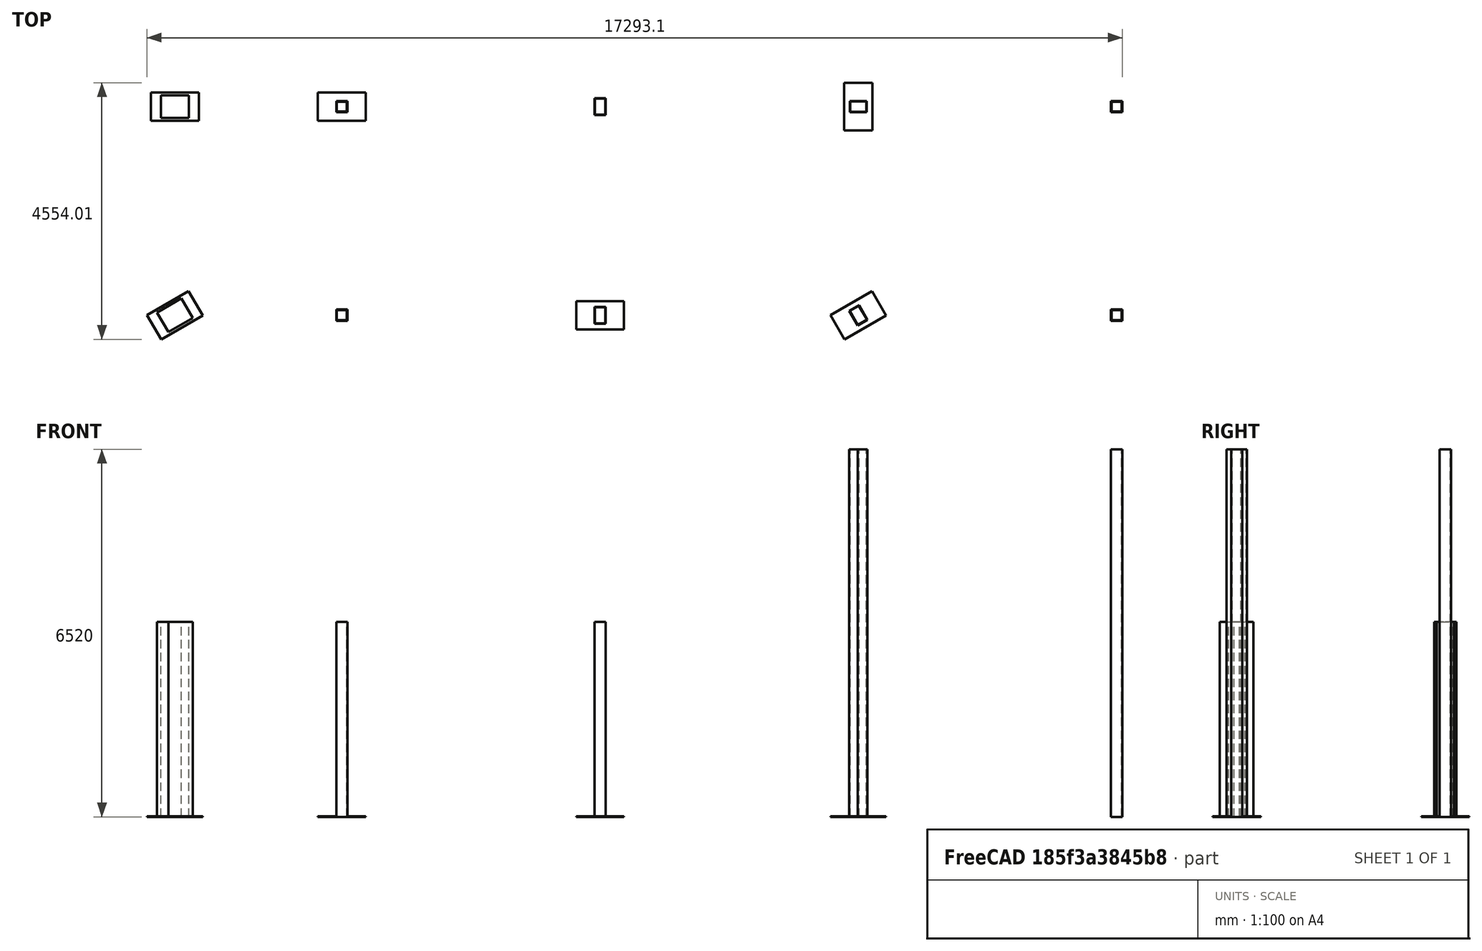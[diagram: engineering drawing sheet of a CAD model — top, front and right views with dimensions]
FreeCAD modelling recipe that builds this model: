
FCSTD DOCUMENT  (FreeCAD 1.0R1234)
Label: base_plate
License: All rights reserved
LicenseURL: http://en.wikipedia.org/wiki/All_rights_reserved
objects: Part::FeaturePython×34, Part::Part2DObjectPython×21, App::FeaturePython×10, App::DocumentObjectGroup×2
note: 147 computed .brp shape members not serialized (recipe doc carries the construction recipe); baked Part::Feature solids carry a one-line shape summary decoded from their .brp

FEATURE [Part::Part2DObjectPython] Line  label="C1_Story1_CenterLine"  # Draft 2D object (typed FeaturePython)
  Area = 0
  ChamferSize = 0
  Closed = false
  End = (30830,27720,3460)
  FilletRadius = 0
  Length = 3460
  MakeFace = true
  Points = (2) [(30830,27720,0),(30830,27720,3460)]
  Start = (30830,27720,0)
  Subdivisions = 0
FEATURE [Part::Part2DObjectPython] COL60X90  # Draft 2D object (typed FeaturePython)
  Height = 500
  Width = 400
FEATURE [Part::Part2DObjectPython] Line001  label="C2_Story1_CenterLine"  # Draft 2D object (typed FeaturePython)
  Area = 0
  ChamferSize = 0
  Closed = false
  End = (30830,31420,3460)
  FilletRadius = 0
  Length = 3460
  MakeFace = true
  Points = (2) [(30830,31420,0),(30830,31420,3460)]
  Start = (30830,31420,0)
  Subdivisions = 0
FEATURE [Part::Part2DObjectPython] Line002  label="C3_Story1_CenterLine"  # Draft 2D object (typed FeaturePython)
  Area = 0
  ChamferSize = 0
  Closed = false
  End = (33790,27720,3460)
  FilletRadius = 0
  Length = 3460
  MakeFace = true
  Points = (2) [(33790,27720,0),(33790,27720,3460)]
  Start = (33790,27720,0)
  Subdivisions = 0
FEATURE [Part::Part2DObjectPython] BOX200X200X12  # Draft 2D object (typed FeaturePython)
  Height = 200
  Thickness = 12
  Width = 200
FEATURE [Part::FeaturePython] Structure002  label="C3_Story1"  # Arch/BIM 24 (typed FeaturePython)
  AttacherType = Attacher::AttachEngine3D
  AttachmentOffset = pos=(0,0,0) rot=(0,0,1;1.5708rad)
  Base = -> BOX200X200X12
  BaseMirror = false
  BaseOffsetX = 0
  BaseOffsetY = 0
  BasePerpendicularToTool = false
  BaseRotation = 0
  ComputedLength = 0
  FaceMaker = 0
  Height = 3460
  HorizontalArea = 9024
  IfcData = attributes={"GlobalId": {"name": "GlobalId", "type": "IfcGloballyUniqueId", "is_enum": false, "enum_values": []}, "Description": {"... (+438 chars omitted),+1 more (map truncated)
  IfcType = 24
  Length = 0
  MapMode = 7
  MoveBase = false
  MoveWithHost = false
  Nodes = (2) [(33790,27720,0),(33790,27720,3460)]
  NodesOffset = 0
  Normal = (0,0,0)
  PerimeterLength = 800
  Placement = pos=(33790,27720,0) rot=(0,0,1;1.5708rad)
  PredefinedType = 0
  Support = -> [Line002]
  ToolOffsetFirst = 0
  ToolOffsetLast = 0
  VerticalArea = 5.20384e+06
  Width = 778
  combos_load = DStlD1=225.648, -2449.4, 2.69,DStlD2=273.2928, -3371.06, -126.35,comb11=315.9072, -3429.16, 3.76,comb21=313.3562, -2587.55, 10.91,+37 more (map truncated)
FEATURE [Part::Part2DObjectPython] Line003  label="C4_Story1_CenterLine"  # Draft 2D object (typed FeaturePython)
  Area = 0
  ChamferSize = 0
  Closed = false
  End = (33790,31420,3460)
  FilletRadius = 0
  Length = 3460
  MakeFace = true
  Points = (2) [(33790,31420,0),(33790,31420,3460)]
  Start = (33790,31420,0)
  Subdivisions = 0
FEATURE [Part::Part2DObjectPython] Line004  label="C5_Story1_CenterLine"  # Draft 2D object (typed FeaturePython)
  Area = 0
  ChamferSize = 0
  Closed = false
  End = (38370,27720,3460)
  FilletRadius = 0
  Length = 3460
  MakeFace = true
  Points = (2) [(38370,27720,0),(38370,27720,3460)]
  Start = (38370,27720,0)
  Subdivisions = 0
FEATURE [Part::Part2DObjectPython] BOX20X30  # Draft 2D object (typed FeaturePython)
  Height = 200
  Thickness = 8
  Width = 300
FEATURE [Part::Part2DObjectPython] Line005  label="C6_Story1_CenterLine"  # Draft 2D object (typed FeaturePython)
  Area = 0
  ChamferSize = 0
  Closed = false
  End = (38370,31420,3460)
  FilletRadius = 0
  Length = 3460
  MakeFace = true
  Points = (2) [(38370,31420,0),(38370,31420,3460)]
  Start = (38370,31420,0)
  Subdivisions = 0
FEATURE [Part::FeaturePython] Structure005  label="C6_Story1"  # Arch/BIM 24 (typed FeaturePython)
  AttacherType = Attacher::AttachEngine3D
  AttachmentOffset = pos=(0,0,0) rot=(0,0,1;1.5708rad)
  Base = -> BOX20X30
  BaseMirror = false
  BaseOffsetX = 0
  BaseOffsetY = 0
  BasePerpendicularToTool = false
  BaseRotation = 0
  ComputedLength = 0
  FaceMaker = 0
  Height = 3460
  HorizontalArea = 7744
  IfcData = attributes={"GlobalId": {"name": "GlobalId", "type": "IfcGloballyUniqueId", "is_enum": false, "enum_values": []}, "Description": {"... (+438 chars omitted),+1 more (map truncated)
  IfcType = 24
  Length = 0
  MapMode = 7
  MoveBase = false
  MoveWithHost = false
  Nodes = (2) [(38370,31420,0),(38370,31420,3460)]
  NodesOffset = 0
  Normal = (0,0,0)
  PerimeterLength = 1000
  Placement = pos=(38370,31420,0) rot=(0,0,1;1.5708rad)
  PredefinedType = 0
  Support = -> [Line005]
  ToolOffsetFirst = 0
  ToolOffsetLast = 0
  VerticalArea = 6.69856e+06
  Width = 778
  combos_load = DStlD1=197.8429, 3076.07, 349.51,DStlD2=245.2578, 4878.87, 1107.77,comb11=276.98, 4306.5, 489.31,comb21=243.6131, 3588.13, 163,+37 more (map truncated)
FEATURE [Part::Part2DObjectPython] Line006  label="C11_Story2_CenterLine"  # Draft 2D object (typed FeaturePython)
  Area = 0
  ChamferSize = 0
  Closed = false
  End = (42950,27720,6520)
  FilletRadius = 0
  Length = 6520
  MakeFace = true
  Points = (2) [(42950,27720,0),(42950,27720,6520)]
  Start = (42950,27720,0)
  Subdivisions = 0
FEATURE [Part::Part2DObjectPython] Line007  label="C12_Story2_CenterLine"  # Draft 2D object (typed FeaturePython)
  Area = 0
  ChamferSize = 0
  Closed = false
  End = (42950,31420,6520)
  FilletRadius = 0
  Length = 6520
  MakeFace = true
  Points = (2) [(42950,31420,0),(42950,31420,6520)]
  Start = (42950,31420,0)
  Subdivisions = 0
FEATURE [Part::Part2DObjectPython] Line008  label="C13_Story2_CenterLine"  # Draft 2D object (typed FeaturePython)
  Area = 0
  ChamferSize = 0
  Closed = false
  End = (47530,27720,6520)
  FilletRadius = 0
  Length = 6520
  MakeFace = true
  Points = (2) [(47530,27720,0),(47530,27720,6520)]
  Start = (47530,27720,0)
  Subdivisions = 0
FEATURE [Part::FeaturePython] Structure008  label="C13_Story2"  # Arch/BIM 24 (typed FeaturePython)
  AttacherType = Attacher::AttachEngine3D
  AttachmentOffset = pos=(0,0,0) rot=(0,0,1;3.14159rad)
  Base = -> BOX200X200X12
  BaseMirror = false
  BaseOffsetX = 0
  BaseOffsetY = 0
  BasePerpendicularToTool = false
  BaseRotation = 0
  ComputedLength = 0
  FaceMaker = 0
  Height = 6520
  HorizontalArea = 9024
  IfcData = attributes={"GlobalId": {"name": "GlobalId", "type": "IfcGloballyUniqueId", "is_enum": false, "enum_values": []}, "Description": {"... (+438 chars omitted),+1 more (map truncated)
  IfcType = 24
  Length = 0
  MapMode = 7
  MoveBase = false
  MoveWithHost = false
  Nodes = (2) [(47530,27720,0),(47530,27720,6520)]
  NodesOffset = 0
  Normal = (0,0,0)
  PerimeterLength = 800
  Placement = pos=(47530,27720,0) rot=(0,0,1;3.14159rad)
  PredefinedType = 0
  Support = -> [Line008]
  ToolOffsetFirst = 0
  ToolOffsetLast = 0
  VerticalArea = 9806080
  Width = 778
  combos_load = DStlD1=130.4832, -1568.85, -477.1,DStlD2=152.9529, -2563.65, 493.5,comb11=182.6765, -2196.39, -667.94,comb21=161.6057, -1832.03, -693.36,+37 more (map truncated)
FEATURE [Part::Part2DObjectPython] Line009  label="C14_Story2_CenterLine"  # Draft 2D object (typed FeaturePython)
  Area = 0
  ChamferSize = 0
  Closed = false
  End = (47530,31420,6520)
  FilletRadius = 0
  Length = 6520
  MakeFace = true
  Points = (2) [(47530,31420,0),(47530,31420,6520)]
  Start = (47530,31420,0)
  Subdivisions = 0
FEATURE [Part::FeaturePython] Structure009  label="C14_Story2"  # Arch/BIM 24 (typed FeaturePython)
  AttacherType = Attacher::AttachEngine3D
  AttachmentOffset = pos=(0,0,0) rot=(0,0,1;1.5708rad)
  Base = -> BOX200X200X12
  BaseMirror = false
  BaseOffsetX = 0
  BaseOffsetY = 0
  BasePerpendicularToTool = false
  BaseRotation = 0
  ComputedLength = 0
  FaceMaker = 0
  Height = 6520
  HorizontalArea = 9024
  IfcData = attributes={"GlobalId": {"name": "GlobalId", "type": "IfcGloballyUniqueId", "is_enum": false, "enum_values": []}, "Description": {"... (+438 chars omitted),+1 more (map truncated)
  IfcType = 24
  Length = 0
  MapMode = 7
  MoveBase = false
  MoveWithHost = false
  Nodes = (2) [(47530,31420,0),(47530,31420,6520)]
  NodesOffset = 0
  Normal = (0,0,0)
  PerimeterLength = 800
  Placement = pos=(47530,31420,0) rot=(0,0,1;1.5708rad)
  PredefinedType = 0
  Support = -> [Line009]
  ToolOffsetFirst = 0
  ToolOffsetLast = 0
  VerticalArea = 9.80608e+06
  Width = 778
  combos_load = DStlD1=130.648, 2043.72, -433.08,DStlD2=153.3261, 3531.07, 565.05,comb11=182.9072, 2861.2, -606.31,comb21=161.7518, 2254.87, -666.26,+37 more (map truncated)
FEATURE [Part::Part2DObjectPython] Line010  # Draft 2D object (typed FeaturePython)
  Area = 0
  ChamferSize = 0
  Closed = false
  End = (47530,31420,0)
  FilletRadius = 0
  Length = 16700
  MakeFace = true
  Points = (2) [(30830,31420,0),(47530,31420,0)]
  Start = (30830,31420,0)
  Subdivisions = 0
FEATURE [Part::FeaturePython] BaseFoundation001  # Arch/BIM 77 (typed FeaturePython)
  Base = -> Line010
  HorizontalArea = 0
  IfcData = attributes={"GlobalId": {"name": "GlobalId", "type": "IfcGloballyUniqueId", "is_enum": false, "enum_values": []}, "Description": {"... (+511 chars omitted),+1 more (map truncated)
  IfcType = 77
  MoveBase = false
  MoveWithHost = false
  PerimeterLength = 0
  PredefinedType = 0
  VerticalArea = 0
  align = 1
  design_type = 0
  fc = 30000
  final_wire_first_point = (0,0,0)
  final_wire_last_point = (0,0,0)
  height = 1100
  ks = 2.3
  layer = 0
  left_width = 500
  right_width = 250
  width = 750
FEATURE [Part::Part2DObjectPython] Line011  # Draft 2D object (typed FeaturePython)
  Area = 0
  ChamferSize = 0
  Closed = false
  End = (47530,27720,0)
  FilletRadius = 0
  Length = 16700
  MakeFace = true
  Points = (2) [(30830,27720,0),(47530,27720,0)]
  Start = (30830,27720,0)
  Subdivisions = 0
FEATURE [Part::FeaturePython] BaseFoundation002  # Arch/BIM 77 (typed FeaturePython)
  Base = -> Line011
  HorizontalArea = 0
  IfcData = attributes={"GlobalId": {"name": "GlobalId", "type": "IfcGloballyUniqueId", "is_enum": false, "enum_values": []}, "Description": {"... (+511 chars omitted),+1 more (map truncated)
  IfcType = 77
  MoveBase = false
  MoveWithHost = false
  PerimeterLength = 0
  PredefinedType = 0
  VerticalArea = 0
  align = 0
  design_type = 0
  fc = 30000
  final_wire_first_point = (0,0,0)
  final_wire_last_point = (0,0,0)
  height = 1100
  ks = 2.3
  layer = 0
  left_width = 500
  right_width = 500
  width = 1000
FEATURE [Part::Part2DObjectPython] Line012  # Draft 2D object (typed FeaturePython)
  Area = 0
  ChamferSize = 0
  Closed = false
  End = (30830,31420,0)
  FilletRadius = 0
  Length = 3700
  MakeFace = true
  Points = (2) [(30830,27720,0),(30830,31420,0)]
  Start = (30830,27720,0)
  Subdivisions = 0
FEATURE [Part::FeaturePython] BaseFoundation003  # Arch/BIM 77 (typed FeaturePython)
  Base = -> Line012
  HorizontalArea = 0
  IfcData = attributes={"GlobalId": {"name": "GlobalId", "type": "IfcGloballyUniqueId", "is_enum": false, "enum_values": []}, "Description": {"... (+511 chars omitted),+1 more (map truncated)
  IfcType = 77
  MoveBase = false
  MoveWithHost = false
  PerimeterLength = 0
  PredefinedType = 0
  VerticalArea = 0
  align = 1
  design_type = 0
  fc = 30000
  final_wire_first_point = (0,0,0)
  final_wire_last_point = (0,0,0)
  height = 1100
  ks = 2.3
  layer = 1
  left_width = 500
  right_width = 250
  width = 750
FEATURE [Part::Part2DObjectPython] Line013  # Draft 2D object (typed FeaturePython)
  Area = 0
  ChamferSize = 0
  Closed = false
  End = (33790,31420,0)
  FilletRadius = 0
  Length = 3700
  MakeFace = true
  Points = (2) [(33790,27720,0),(33790,31420,0)]
  Start = (33790,27720,0)
  Subdivisions = 0
FEATURE [Part::FeaturePython] BaseFoundation004  # Arch/BIM 77 (typed FeaturePython)
  Base = -> Line013
  HorizontalArea = 0
  IfcData = attributes={"GlobalId": {"name": "GlobalId", "type": "IfcGloballyUniqueId", "is_enum": false, "enum_values": []}, "Description": {"... (+511 chars omitted),+1 more (map truncated)
  IfcType = 77
  MoveBase = false
  MoveWithHost = false
  PerimeterLength = 0
  PredefinedType = 0
  VerticalArea = 0
  align = 1
  design_type = 0
  fc = 30000
  final_wire_first_point = (0,0,0)
  final_wire_last_point = (0,0,0)
  height = 1100
  ks = 2.3
  layer = 1
  left_width = 500
  right_width = 250
  width = 750
FEATURE [Part::Part2DObjectPython] Line014  # Draft 2D object (typed FeaturePython)
  Area = 0
  ChamferSize = 0
  Closed = false
  End = (38370,27720,0)
  FilletRadius = 0
  Length = 3700
  MakeFace = true
  Points = (2) [(38370,31420,0),(38370,27720,0)]
  Start = (38370,31420,0)
  Subdivisions = 0
FEATURE [Part::FeaturePython] BaseFoundation005  # Arch/BIM 77 (typed FeaturePython)
  Base = -> Line014
  HorizontalArea = 0
  IfcData = attributes={"GlobalId": {"name": "GlobalId", "type": "IfcGloballyUniqueId", "is_enum": false, "enum_values": []}, "Description": {"... (+511 chars omitted),+1 more (map truncated)
  IfcType = 77
  MoveBase = false
  MoveWithHost = false
  PerimeterLength = 0
  PredefinedType = 0
  VerticalArea = 0
  align = 1
  design_type = 0
  fc = 30000
  final_wire_first_point = (0,0,0)
  final_wire_last_point = (0,0,0)
  height = 1100
  ks = 2.3
  layer = 1
  left_width = 500
  right_width = 250
  width = 750
FEATURE [Part::Part2DObjectPython] Line015  # Draft 2D object (typed FeaturePython)
  Area = 0
  ChamferSize = 0
  Closed = false
  End = (42950,31420,0)
  FilletRadius = 0
  Length = 3700
  MakeFace = true
  Points = (2) [(42950,27720,0),(42950,31420,0)]
  Start = (42950,27720,0)
  Subdivisions = 0
FEATURE [Part::FeaturePython] BaseFoundation006  # Arch/BIM 77 (typed FeaturePython)
  Base = -> Line015
  HorizontalArea = 0
  IfcData = attributes={"GlobalId": {"name": "GlobalId", "type": "IfcGloballyUniqueId", "is_enum": false, "enum_values": []}, "Description": {"... (+511 chars omitted),+1 more (map truncated)
  IfcType = 77
  MoveBase = false
  MoveWithHost = false
  PerimeterLength = 0
  PredefinedType = 0
  VerticalArea = 0
  align = 1
  design_type = 0
  fc = 30000
  final_wire_first_point = (0,0,0)
  final_wire_last_point = (0,0,0)
  height = 1100
  ks = 2.3
  layer = 1
  left_width = 500
  right_width = 250
  width = 750
FEATURE [Part::Part2DObjectPython] Line016  # Draft 2D object (typed FeaturePython)
  Area = 0
  ChamferSize = 0
  Closed = false
  End = (47530,27720,0)
  FilletRadius = 0
  Length = 3700
  MakeFace = true
  Points = (2) [(47530,31420,0),(47530,27720,0)]
  Start = (47530,31420,0)
  Subdivisions = 0
FEATURE [Part::FeaturePython] BaseFoundation007  # Arch/BIM 77 (typed FeaturePython)
  Base = -> Line016
  HorizontalArea = 0
  IfcData = attributes={"GlobalId": {"name": "GlobalId", "type": "IfcGloballyUniqueId", "is_enum": false, "enum_values": []}, "Description": {"... (+511 chars omitted),+1 more (map truncated)
  IfcType = 77
  MoveBase = false
  MoveWithHost = false
  PerimeterLength = 0
  PredefinedType = 0
  VerticalArea = 0
  align = 1
  design_type = 0
  fc = 30000
  final_wire_first_point = (0,0,0)
  final_wire_last_point = (0,0,0)
  height = 1100
  ks = 2.3
  layer = 1
  left_width = 500
  right_width = 250
  width = 750
FEATURE [Part::FeaturePython] Foundation  # Arch/BIM 77 (typed FeaturePython)
  HorizontalArea = 0
  IfcType = 77
  MoveBase = false
  MoveWithHost = false
  PerimeterLength = 0
  VerticalArea = 0
  base_foundations = -> [BaseFoundation001,BaseFoundation002,BaseFoundation003,BaseFoundation004,BaseFoundation005,BaseFoundation006,BaseFoundation007]
  continuous_layer = 0
  cover = 75
  d = 1025
  fc = 25000
  foundation_type = 0
  height = 0
  height_punch = 1100
  ks = 2
  level = 0
  redraw = false
  split = true
  volume = 46.2413
FEATURE [Part::FeaturePython] BasePlate  # WARN: FeaturePython — macro-defined, semantics opaque (R4)
  Bx = 850
  By = 500
  Placement = pos=(30405,31170,0) rot=(0,0,1;0rad)
  Thickness = 10
FEATURE [Part::FeaturePython] Structure001  label="C2_Story1"  # Arch/BIM 24 (typed FeaturePython)
  AttacherType = Attacher::AttachEngine3D
  AttachmentOffset = pos=(0,0,0) rot=(0,0,1;1.5708rad)
  Base = -> COL60X90
  BaseMirror = false
  BaseOffsetX = 0
  BaseOffsetY = 0
  BasePerpendicularToTool = false
  BaseRotation = 0
  ComputedLength = 3460
  FaceMaker = 0
  Height = 3460
  HorizontalArea = 200000
  IfcData = attributes={"GlobalId": {"name": "GlobalId", "type": "IfcGloballyUniqueId", "is_enum": false, "enum_values": []}, "Description": {"... (+438 chars omitted),+1 more (map truncated)
  IfcType = 24
  Length = 0
  MapMode = 7
  MoveBase = false
  MoveWithHost = false
  Nodes = (2) [(30830,31420,0),(30830,31420,3460)]
  NodesOffset = 0
  Normal = (0,0,0)
  PerimeterLength = 1800
  Placement = pos=(30830,31420,0) rot=(0,0,1;1.5708rad)
  PredefinedType = 0
  Support = -> [Line001]
  ToolOffsetFirst = 0
  ToolOffsetLast = 0
  VerticalArea = 6.228e+06
  Width = 778
  base_plate = -> BasePlate
  combos_load = DStlD1=151.181, 1795.23, -5462.01,DStlD2=179.6834, 1446.54, -6639.16,comb11=211.6534, 2513.33, -7646.82,comb21=230.1113, 1796.2, -6880.14,+37 more (map truncated)
FEATURE [Part::FeaturePython] BasePlate001  # WARN: FeaturePython — macro-defined, semantics opaque (R4)
  Bx = 850
  By = 500
  Placement = pos=(33365,31170,0) rot=(0,0,1;0rad)
  Thickness = 10
FEATURE [Part::FeaturePython] Structure003  label="C4_Story1"  # Arch/BIM 24 (typed FeaturePython)
  AttacherType = Attacher::AttachEngine3D
  AttachmentOffset = pos=(0,0,0) rot=(0,0,1;1.5708rad)
  Base = -> BOX200X200X12
  BaseMirror = false
  BaseOffsetX = 0
  BaseOffsetY = 0
  BasePerpendicularToTool = false
  BaseRotation = 0
  ComputedLength = 3460
  FaceMaker = 0
  Height = 3460
  HorizontalArea = 9024
  IfcData = attributes={"GlobalId": {"name": "GlobalId", "type": "IfcGloballyUniqueId", "is_enum": false, "enum_values": []}, "Description": {"... (+438 chars omitted),+1 more (map truncated)
  IfcType = 24
  Length = 0
  MapMode = 7
  MoveBase = false
  MoveWithHost = false
  Nodes = (2) [(33790,31420,0),(33790,31420,3460)]
  NodesOffset = 0
  Normal = (0,0,0)
  PerimeterLength = 800
  Placement = pos=(33790,31420,0) rot=(0,0,1;1.5708rad)
  PredefinedType = 0
  Support = -> [Line003]
  ToolOffsetFirst = 0
  ToolOffsetLast = 0
  VerticalArea = 5.20384e+06
  Width = 778
  base_plate = -> BasePlate001
  combos_load = DStlD1=233.3753, 2703.39, -578.57,DStlD2=285.8309, 3842.47, -1053.16,comb11=326.7254, 3784.74, -810,comb21=330.41, 3143.79, -1379.53,+37 more (map truncated)
FEATURE [Part::FeaturePython] BasePlate002  # WARN: FeaturePython — macro-defined, semantics opaque (R4)
  Bx = 850
  By = 500
  Placement = pos=(30586.9,27291,0) rot=(0,0,1;0.523599rad)
  Thickness = 10
FEATURE [Part::FeaturePython] Structure  label="C1_Story1"  # Arch/BIM 24 (typed FeaturePython)
  AttacherType = Attacher::AttachEngine3D
  AttachmentOffset = pos=(0,0,0) rot=(0,0,1;2.0944rad)
  Base = -> COL60X90
  BaseMirror = false
  BaseOffsetX = 0
  BaseOffsetY = 0
  BasePerpendicularToTool = false
  BaseRotation = 0
  ComputedLength = 3460
  FaceMaker = 0
  Height = 3460
  HorizontalArea = 200000
  IfcData = attributes={"GlobalId": {"name": "GlobalId", "type": "IfcGloballyUniqueId", "is_enum": false, "enum_values": []}, "Description": {"... (+438 chars omitted),+1 more (map truncated)
  IfcType = 24
  Length = 0
  MapMode = 7
  MoveBase = false
  MoveWithHost = false
  Nodes = (2) [(30830,27720,0),(30830,27720,3460)]
  NodesOffset = 0
  Normal = (0,0,0)
  PerimeterLength = 1800
  Placement = pos=(30830,27720,0) rot=(0,0,1;2.0944rad)
  PredefinedType = 0
  Support = -> [Line]
  ToolOffsetFirst = 0
  ToolOffsetLast = 0
  VerticalArea = 6228000
  Width = 778
  base_plate = -> BasePlate002
  combos_load = DStlD1=142.0558, -1171.01, -6154.41,DStlD2=164.7691, -629.86, -8214.2,comb11=198.8782, -1639.41, -8616.17,comb21=210.0626, -788.63, -8257.61,+37 more (map truncated)
FEATURE [Part::FeaturePython] BasePlate003  # WARN: FeaturePython — macro-defined, semantics opaque (R4)
  Bx = 850
  By = 500
  Placement = pos=(37945,27470,0) rot=(0,0,1;0rad)
  Thickness = 10
FEATURE [Part::FeaturePython] Structure004  label="C5_Story1"  # Arch/BIM 24 (typed FeaturePython)
  AttacherType = Attacher::AttachEngine3D
  AttachmentOffset = pos=(0,0,0) rot=(0,0,1;1.5708rad)
  Base = -> BOX20X30
  BaseMirror = false
  BaseOffsetX = 0
  BaseOffsetY = 0
  BasePerpendicularToTool = false
  BaseRotation = 0
  ComputedLength = 3460
  FaceMaker = 0
  Height = 3460
  HorizontalArea = 7744
  IfcData = attributes={"GlobalId": {"name": "GlobalId", "type": "IfcGloballyUniqueId", "is_enum": false, "enum_values": []}, "Description": {"... (+438 chars omitted),+1 more (map truncated)
  IfcType = 24
  Length = 0
  MapMode = 7
  MoveBase = false
  MoveWithHost = false
  Nodes = (2) [(38370,27720,0),(38370,27720,3460)]
  NodesOffset = 0
  Normal = (0,0,0)
  PerimeterLength = 1000
  Placement = pos=(38370,27720,0) rot=(0,0,1;1.5708rad)
  PredefinedType = 0
  Support = -> [Line004]
  ToolOffsetFirst = 0
  ToolOffsetLast = 0
  VerticalArea = 6.69856e+06
  Width = 778
  base_plate = -> BasePlate003
  combos_load = DStlD1=197.8877, -2977.26, 349.01,DStlD2=245.1856, -4571.89, 1099.63,comb11=277.0428, -4168.16, 488.61,comb21=243.8168, -3776.3, 259.56,+37 more (map truncated)
FEATURE [Part::FeaturePython] BasePlate004  # WARN: FeaturePython — macro-defined, semantics opaque (R4)
  Bx = 850
  By = 500
  Placement = pos=(43200,30995,0) rot=(0,0,1;1.5708rad)
  Thickness = 10
FEATURE [Part::FeaturePython] Structure007  label="C12_Story2"  # Arch/BIM 24 (typed FeaturePython)
  AttacherType = Attacher::AttachEngine3D
  AttachmentOffset = pos=(0,0,0) rot=(0,0,1;3.14159rad)
  Base = -> BOX20X30
  BaseMirror = false
  BaseOffsetX = 0
  BaseOffsetY = 0
  BasePerpendicularToTool = false
  BaseRotation = 0
  ComputedLength = 6520
  FaceMaker = 0
  Height = 6520
  HorizontalArea = 7744
  IfcData = attributes={"GlobalId": {"name": "GlobalId", "type": "IfcGloballyUniqueId", "is_enum": false, "enum_values": []}, "Description": {"... (+438 chars omitted),+1 more (map truncated)
  IfcType = 24
  Length = 0
  MapMode = 7
  MoveBase = false
  MoveWithHost = false
  Nodes = (2) [(42950,31420,0),(42950,31420,6520)]
  NodesOffset = 0
  Normal = (0,0,0)
  PerimeterLength = 1000
  Placement = pos=(42950,31420,0) rot=(0,0,1;3.14159rad)
  PredefinedType = 0
  Support = -> [Line007]
  ToolOffsetFirst = 0
  ToolOffsetLast = 0
  VerticalArea = 12622720
  Width = 778
  base_plate = -> BasePlate004
  combos_load = DStlD1=135.9336, 1090.77, -4062.46,DStlD2=160.4971, 2407.81, -7237.03,comb11=190.307, 1527.08, -5687.44,comb21=169.3985, 1155.8, -4747.91,+37 more (map truncated)
FEATURE [Part::FeaturePython] BasePlate005  # WARN: FeaturePython — macro-defined, semantics opaque (R4)
  Bx = 850
  By = 500
  Placement = pos=(42706.9,27291,0) rot=(0,0,1;0.523599rad)
  Thickness = 10
FEATURE [Part::FeaturePython] Structure006  label="C11_Story2"  # Arch/BIM 24 (typed FeaturePython)
  AttacherType = Attacher::AttachEngine3D
  AttachmentOffset = pos=(0,0,0) rot=(0,0,1;2.0944rad)
  Base = -> BOX20X30
  BaseMirror = false
  BaseOffsetX = 0
  BaseOffsetY = 0
  BasePerpendicularToTool = false
  BaseRotation = 0
  ComputedLength = 6520
  FaceMaker = 0
  Height = 6520
  HorizontalArea = 7744
  IfcData = attributes={"GlobalId": {"name": "GlobalId", "type": "IfcGloballyUniqueId", "is_enum": false, "enum_values": []}, "Description": {"... (+438 chars omitted),+1 more (map truncated)
  IfcType = 24
  Length = 0
  MapMode = 7
  MoveBase = false
  MoveWithHost = false
  Nodes = (2) [(42950,27720,0),(42950,27720,6520)]
  NodesOffset = 0
  Normal = (0,0,0)
  PerimeterLength = 1000
  Placement = pos=(42950,27720,0) rot=(0,0,1;2.0944rad)
  PredefinedType = 0
  Support = -> [Line006]
  ToolOffsetFirst = 0
  ToolOffsetLast = 0
  VerticalArea = 12622720
  Width = 778
  base_plate = -> BasePlate005
  combos_load = DStlD1=136.3534, -1862.15, -3050.35,DStlD2=161.5432, -3826.86, -5611.4,comb11=190.8948, -2607.01, -4270.49,comb21=169.8844, -2099.39, -3515.7,+37 more (map truncated)
FEATURE [App::DocumentObjectGroup] Columns
  Group = -> [Structure,Structure001,Structure002,Structure003,Structure004,Structure005,Structure006,Structure007,Structure008,Structure009]
FEATURE [App::FeaturePython] Text  # WARN: FeaturePython — macro-defined, semantics opaque (R4)
  Placement = pos=(30330,27968,3460) rot=(0,0,1;0.523599rad)
  Text = Corner 1 | 0.16
FEATURE [Part::FeaturePython] Punch  # WARN: FeaturePython — macro-defined, semantics opaque (R4)
  Area = 2.31931e+06
  Av = 400
  Fys = 340000
  I22 = 1.01206e+12
  I23 = 0
  I33 = 3.4054e+11
  Location = 0
  Ratio = 0.16
  Use_Reinforcement = false
  Vc = 2.89914e+09
  Vs = 0
  Vu = 4.63862e+08
  alpha_s = 20
  angle = 30
  b0 = 2262.74
  bx = 675
  by = 450
  center_of_column = (30830,27720,0)
  center_of_load = (30830,27720,0)
  center_of_punch = (31389.9,27697.1,-512.5)
  column = -> Structure
  combos_ratio = DStlD1=0.07,DStlD2=0.09,Max=0.16,comb11=0.10,comb21=0.11,comb22=0.11,comb31=0.10,comb32=0.10,comb41=0.10,comb42=0.10,comb51=0.09,comb510=0.06,+30 more (map truncated)
  d = 1025
  fc = 25000
  foundation = -> Foundation
  gamma_vx = 0.35247
  gamma_vy = 0.44949
  id = C1_Story1
  one_way_shear_capacity = 1.44957e+09
  s = 0
  text = -> Text
  user_location = false
  vc = 1250
  x = 0
FEATURE [App::FeaturePython] Text001  # WARN: FeaturePython — macro-defined, semantics opaque (R4)
  Placement = pos=(30330,31301.2,3460) rot=(0,0,1;0rad)
  Text = Corner 4 | 0.25
FEATURE [Part::FeaturePython] Punch001  # WARN: FeaturePython — macro-defined, semantics opaque (R4)
  Area = 1537500
  Av = 400
  Fys = 340000
  I22 = 3.8928e+11
  I23 = 0
  I33 = 4.68737e+11
  Location = 3
  Ratio = 0.25
  Use_Reinforcement = false
  Vc = 1921875000
  Vs = 0
  Vu = 476625000
  alpha_s = 20
  angle = 0
  b0 = 1500
  bx = 675
  by = 450
  center_of_column = (30830,31420,0)
  center_of_load = (30830,31420,0)
  center_of_punch = (31192.5,31113.8,-512.5)
  column = -> Structure001
  combos_ratio = DStlD1=0.12,DStlD2=0.14,Max=0.25,comb11=0.16,comb21=0.18,comb22=0.18,comb31=0.17,comb32=0.16,comb41=0.16,comb42=0.16,comb51=0.21,comb510=0.22,+30 more (map truncated)
  d = 1025
  fc = 25000
  foundation = -> Foundation
  gamma_vx = 0.35247
  gamma_vy = 0.44949
  id = C2_Story1
  one_way_shear_capacity = 960937500
  s = 0
  text = -> Text001
  user_location = false
  vc = 1250
  x = 0
FEATURE [App::FeaturePython] Text002  # WARN: FeaturePython — macro-defined, semantics opaque (R4)
  Placement = pos=(33790,27220,3460) rot=(0,0,1;0rad)
  Text = Edge 1 | 0.15
FEATURE [Part::FeaturePython] Punch002  # WARN: FeaturePython — macro-defined, semantics opaque (R4)
  Area = 2.81875e+06
  Av = 400
  Fys = 340000
  I22 = 5.60062e+11
  I23 = 2.40878e+11
  I33 = 8.81147e+11
  Location = 4
  Ratio = 0.15
  Use_Reinforcement = false
  Vc = 3.52344e+09
  Vs = 0
  Vu = 5.35562e+08
  alpha_s = 30
  angle = 0
  b0 = 2750
  bx = 200
  by = 200
  center_of_column = (33790,27720,0)
  center_of_load = (33790,27720,0)
  center_of_punch = (33755.9,27887,-512.5)
  column = -> Structure002
  combos_ratio = DStlD1=0.07,DStlD2=0.09,Max=0.15,comb11=0.10,comb21=0.10,comb22=0.10,comb31=0.10,comb32=0.10,comb41=0.10,comb42=0.10,comb51=0.11,comb510=0.07,+30 more (map truncated)
  d = 1025
  fc = 25000
  foundation = -> Foundation
  gamma_vx = 0.4
  gamma_vy = 0.4
  id = C3_Story1
  one_way_shear_capacity = 1.76172e+09
  s = 0
  text = -> Text002
  user_location = false
  vc = 1250
  x = 0
FEATURE [App::FeaturePython] Text003  # WARN: FeaturePython — macro-defined, semantics opaque (R4)
  Placement = pos=(33790,31920,3460) rot=(0,0,1;0rad)
  Text = Edge 3 | 0.21
FEATURE [Part::FeaturePython] Punch003  # WARN: FeaturePython — macro-defined, semantics opaque (R4)
  Area = 2306250
  Av = 400
  Fys = 340000
  I22 = 545011718750
  I23 = 3.57415e+11
  I33 = 1.03481e+12
  Location = 6
  Ratio = 0.21
  Use_Reinforcement = false
  Vc = 2882812500
  Vs = 0
  Vu = 599625000
  alpha_s = 30
  angle = 0
  b0 = 2250
  bx = 525
  by = 350
  center_of_column = (33790,31420,0)
  center_of_load = (33790,31420,0)
  center_of_punch = (33748.3,31274.2,-512.5)
  column = -> Structure003
  combos_ratio = DStlD1=0.10,DStlD2=0.12,Max=0.21,comb11=0.14,comb21=0.14,comb22=0.14,comb31=0.14,comb32=0.14,comb41=0.14,comb42=0.14,comb51=0.17,comb510=0.19,+30 more (map truncated)
  d = 1025
  fc = 25000
  foundation = -> Foundation
  gamma_vx = 0.35247
  gamma_vy = 0.44949
  id = C4_Story1
  one_way_shear_capacity = 1441406250
  s = 0
  text = -> Text003
  user_location = false
  vc = 1250
  x = 0
FEATURE [App::FeaturePython] Text004  # WARN: FeaturePython — macro-defined, semantics opaque (R4)
  Placement = pos=(38370,27220,3460) rot=(0,0,1;0rad)
  Text = Edge 1 | 0.16
FEATURE [Part::FeaturePython] Punch004  # WARN: FeaturePython — macro-defined, semantics opaque (R4)
  Area = 2.81875e+06
  Av = 400
  Fys = 340000
  I22 = 6.34141e+11
  I23 = 3.44937e+11
  I33 = 1.34336e+12
  Location = 4
  Ratio = 0.16
  Use_Reinforcement = false
  Vc = 3.52344e+09
  Vs = 0
  Vu = 5.6375e+08
  alpha_s = 30
  angle = 0
  b0 = 2750
  bx = 525
  by = 400
  center_of_column = (38370,27720,0)
  center_of_load = (38370,27720,0)
  center_of_punch = (38404.1,27914.3,-512.5)
  column = -> Structure004
  combos_ratio = DStlD1=0.06,DStlD2=0.08,Max=0.16,comb11=0.10,comb21=0.08,comb22=0.08,comb31=0.09,comb32=0.09,comb41=0.09,comb42=0.09,comb51=0.08,comb510=0.06,+30 more (map truncated)
  d = 1025
  fc = 25000
  foundation = -> Foundation
  gamma_vx = 0.367855
  gamma_vy = 0.43303
  id = C5_Story1
  one_way_shear_capacity = 1.76172e+09
  s = 0
  text = -> Text004
  user_location = false
  vc = 1250
  x = 0
FEATURE [App::FeaturePython] Text005  # WARN: FeaturePython — macro-defined, semantics opaque (R4)
  Placement = pos=(38370,31920,3460) rot=(0,0,1;0rad)
  Text = Edge 3 | 0.22
FEATURE [Part::FeaturePython] Punch005  # WARN: FeaturePython — macro-defined, semantics opaque (R4)
  Area = 2306250
  Av = 400
  Fys = 340000
  I22 = 524511718750
  I23 = 2.80834e+11
  I33 = 6.88151e+11
  Location = 6
  Ratio = 0.22
  Use_Reinforcement = false
  Vc = 2882812500
  Vs = 0
  Vu = 622687500
  alpha_s = 30
  angle = 0
  b0 = 2250
  bx = 200
  by = 300
  center_of_column = (38370,31420,0)
  center_of_load = (38370,31420,0)
  center_of_punch = (38411.7,31282.5,-512.5)
  column = -> Structure005
  combos_ratio = DStlD1=0.08,DStlD2=0.10,Max=0.22,comb11=0.11,comb21=0.10,comb22=0.10,comb31=0.11,comb32=0.10,comb41=0.10,comb42=0.10,comb51=0.14,comb510=0.22,+30 more (map truncated)
  d = 1025
  fc = 25000
  foundation = -> Foundation
  gamma_vx = 0.44949
  gamma_vy = 0.35247
  id = C6_Story1
  one_way_shear_capacity = 1441406250
  s = 0
  text = -> Text005
  user_location = false
  vc = 1250
  x = 0
FEATURE [App::FeaturePython] Text006  # WARN: FeaturePython — macro-defined, semantics opaque (R4)
  Placement = pos=(42950,27220,6520) rot=(0,0,1;0.523599rad)
  Text = Edge 1 | 0.14
FEATURE [Part::FeaturePython] Punch006  # WARN: FeaturePython — macro-defined, semantics opaque (R4)
  Area = 3.72348e+06
  Av = 400
  Fys = 340000
  I22 = 1.30599e+12
  I23 = 8.55785e+11
  I33 = 1.62504e+12
  Location = 4
  Ratio = 0.14
  Use_Reinforcement = false
  Vc = 4.65435e+09
  Vs = 0
  Vu = 6.32991e+08
  alpha_s = 30
  angle = 30
  b0 = 3632.66
  bx = 525
  by = 400
  center_of_column = (42950,27720,0)
  center_of_load = (42950,27720,0)
  center_of_punch = (43013.7,27889.9,-512.5)
  column = -> Structure006
  combos_ratio = DStlD1=0.04,DStlD2=0.05,Max=0.14,comb11=0.06,comb21=0.06,comb22=0.05,comb31=0.06,comb32=0.06,comb41=0.06,comb42=0.06,comb51=0.04,comb510=0.06,+30 more (map truncated)
  d = 1025
  fc = 25000
  foundation = -> Foundation
  gamma_vx = 0.367855
  gamma_vy = 0.43303
  id = C11_Story2
  one_way_shear_capacity = 2.32717e+09
  s = 0
  text = -> Text006
  user_location = false
  vc = 1250
  x = 0
FEATURE [App::FeaturePython] Text007  # WARN: FeaturePython — macro-defined, semantics opaque (R4)
  Placement = pos=(42950,31920,6520) rot=(0,0,1;1.5708rad)
  Text = Edge 3 | 0.14
FEATURE [Part::FeaturePython] Punch007  # WARN: FeaturePython — macro-defined, semantics opaque (R4)
  Area = 2306250
  Av = 400
  Fys = 340000
  I22 = 8.9187e+11
  I23 = 3.67078e+11
  I33 = 621806640625
  Location = 6
  Ratio = 0.14
  Use_Reinforcement = false
  Vc = 2882812500
  Vs = 0
  Vu = 415125000
  alpha_s = 30
  angle = 90
  b0 = 2250
  bx = 525
  by = 400
  center_of_column = (42950,31420,0)
  center_of_load = (42950,31420,0)
  center_of_punch = (42775,31461.7,-512.5)
  column = -> Structure007
  combos_ratio = DStlD1=0.06,DStlD2=0.07,Max=0.14,comb11=0.08,comb21=0.07,comb22=0.07,comb31=0.08,comb32=0.07,comb41=0.08,comb42=0.07,comb51=0.10,comb510=0.14,+30 more (map truncated)
  d = 1025
  fc = 25000
  foundation = -> Foundation
  gamma_vx = 0.367855
  gamma_vy = 0.43303
  id = C12_Story2
  one_way_shear_capacity = 1441406250
  s = 0
  text = -> Text007
  user_location = false
  vc = 1250
  x = 0
FEATURE [App::FeaturePython] Text008  # WARN: FeaturePython — macro-defined, semantics opaque (R4)
  Placement = pos=(48030,27776.2,6520) rot=(0,0,1;1.5708rad)
  Text = Corner 2 | 0.22
FEATURE [Part::FeaturePython] Punch008  # WARN: FeaturePython — macro-defined, semantics opaque (R4)
  Area = 1.79375e+06
  Av = 400
  Fys = 340000
  I22 = 3.42271e+11
  I23 = 0
  I33 = 3.39958e+11
  Location = 1
  Ratio = 0.22
  Use_Reinforcement = false
  Vc = 2.24219e+09
  Vs = 0
  Vu = 4.84313e+08
  alpha_s = 20
  angle = 90
  b0 = 1750
  bx = 200
  by = 200
  center_of_column = (47530,27720,0)
  center_of_load = (47530,27720,0)
  center_of_punch = (47792.5,28016.4,-512.5)
  column = -> Structure008
  combos_ratio = DStlD1=0.09,DStlD2=0.10,Max=0.22,comb11=0.12,comb21=0.10,comb22=0.10,comb31=0.12,comb32=0.11,comb41=0.11,comb42=0.11,comb51=0.10,comb510=0.06,+30 more (map truncated)
  d = 1025
  fc = 25000
  foundation = -> Foundation
  gamma_vx = 0.4
  gamma_vy = 0.4
  id = C13_Story2
  one_way_shear_capacity = 1.12109e+09
  s = 0
  text = -> Text008
  user_location = false
  vc = 1250
  x = 0
FEATURE [App::FeaturePython] Text009  # WARN: FeaturePython — macro-defined, semantics opaque (R4)
  Placement = pos=(48030,31363.8,6520) rot=(0,0,1;0rad)
  Text = Corner 3 | 0.23
FEATURE [Part::FeaturePython] Punch009  # WARN: FeaturePython — macro-defined, semantics opaque (R4)
  Area = 1537500
  Av = 400
  Fys = 340000
  I22 = 3.12405e+11
  I23 = 0
  I33 = 3.12405e+11
  Location = 2
  Ratio = 0.23
  Use_Reinforcement = false
  Vc = 1921875000
  Vs = 0
  Vu = 4.45875e+08
  alpha_s = 20
  angle = 0
  b0 = 1500
  bx = 200
  by = 200
  center_of_column = (47530,31420,0)
  center_of_load = (47530,31420,0)
  center_of_punch = (47286.2,31176.2,-512.5)
  column = -> Structure009
  combos_ratio = DStlD1=0.10,DStlD2=0.11,Max=0.23,comb11=0.13,comb21=0.11,comb22=0.11,comb31=0.13,comb32=0.12,comb41=0.12,comb42=0.12,comb51=0.16,comb510=0.23,+30 more (map truncated)
  d = 1025
  fc = 25000
  foundation = -> Foundation
  gamma_vx = 0.4
  gamma_vy = 0.4
  id = C14_Story2
  one_way_shear_capacity = 960937500
  s = 0
  text = -> Text009
  user_location = false
  vc = 1250
  x = 0
FEATURE [App::DocumentObjectGroup] Punches
  Group = -> [Punch,Punch001,Punch002,Punch003,Punch004,Punch005,Punch006,Punch007,Punch008,Punch009]
FEATURE [Part::Part2DObjectPython] Line017  # Draft 2D object (typed FeaturePython)
  Area = 0
  ChamferSize = 0
  Closed = false
  End = (33790,31420,0)
  FilletRadius = 0
  Length = 2960
  MakeFace = true
  Points = (2) [(30830,31420,0),(33790,31420,0)]
  Start = (30830,31420,0)
  Subdivisions = 0
  type = Beam
